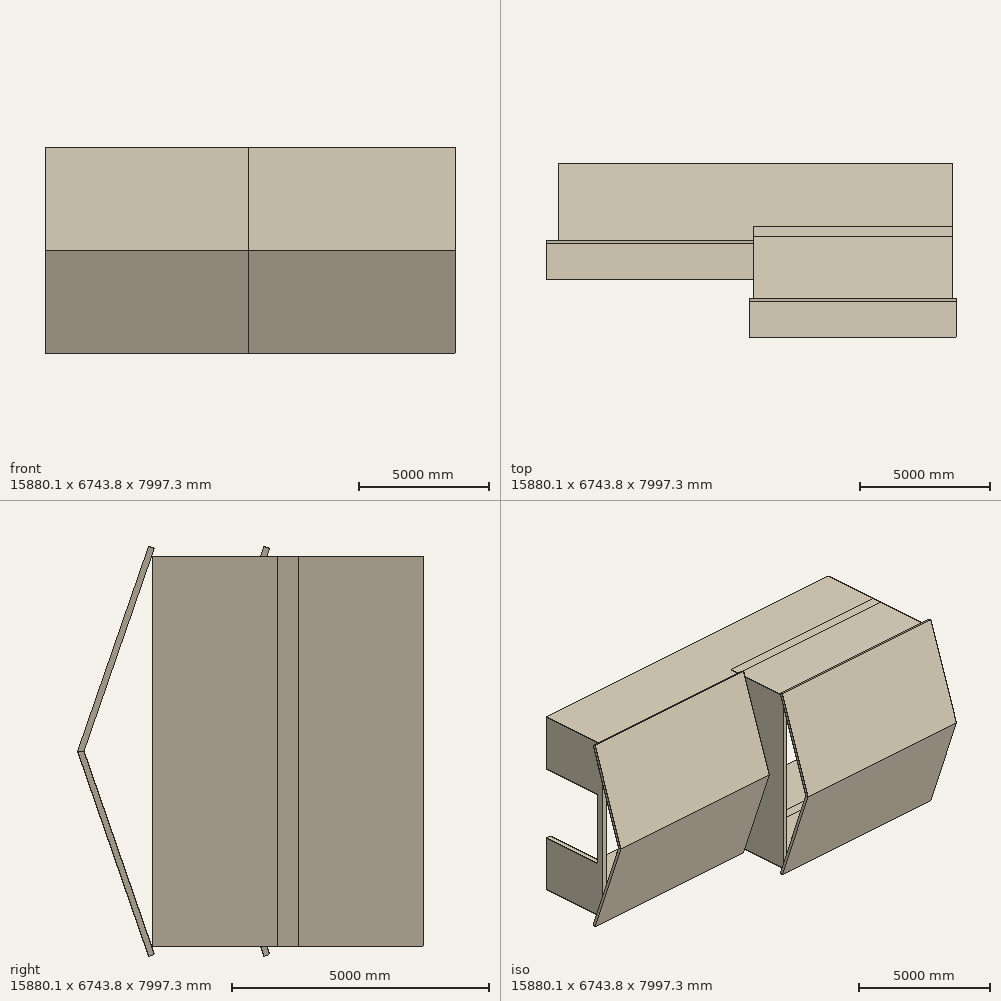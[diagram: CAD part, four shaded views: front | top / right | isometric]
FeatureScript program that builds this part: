
annotation { "Feature Type Name" : "Feature", "Feature Type Description" : "" }
export const myFeature = defineFeature(function(context is Context, id is Id, definition is map)
    precondition{}
    {
        {
            var Q0;
            Q0=qCreatedBy(makeId("Front.planeOp"),FACE);
            var sketch = newSketch(context, id + "F0", { "sketchPlane" : qUnion([Q0])});
            skLineSegment(sketch, "E0.bottom", {"start": v(7620, -3810) * mm, "end": v(-7620, -3810) * mm});
            skLineSegment(sketch, "E0.top", {"start": v(7620, 3810) * mm, "end": v(-7620, 3810) * mm});
            skLineSegment(sketch, "E0.left", {"start": v(7620, -3810) * mm, "end": v(7620, 3810) * mm});
            skLineSegment(sketch, "E0.right", {"start": v(-7620, -3810) * mm, "end": v(-7620, 3810) * mm});
            skPoint(sketch, "E0.middle", {"position": v(0, 0) * mm});
            skLineSegment(sketch, "E1.bottom", {"start": v(7416.8, -3606.8) * mm, "end": v(-7416.8, -3606.8) * mm});
            skLineSegment(sketch, "E1.top", {"start": v(7416.8, 3606.8) * mm, "end": v(-7416.8, 3606.8) * mm});
            skLineSegment(sketch, "E1.left", {"start": v(7416.8, -3606.8) * mm, "end": v(7416.8, 3606.8) * mm});
            skLineSegment(sketch, "E1.right", {"start": v(-7416.8, -3606.8) * mm, "end": v(-7416.8, 3606.8) * mm});
            skLineSegment(sketch, "E2", {"start": v(-76.2, 3810) * mm, "end": v(-76.2, -3810) * mm});
            skLineSegment(sketch, "E3", {"start": v(76.2, 3810) * mm, "end": v(76.2, -3810) * mm});
            skSolve(sketch);
        }
        {
            var Q0;
            {var subQ4=sQuery(id+"F0.wireOp",EDGE,"E0.right");Q0=makeQuery(id+"F0.imprint","IMPRINT",FACE,{"disambiguationData":[TD([[makeQuery(id+"F0.imprint","IMPRINT",EDGE,{"derivedFrom":subQ4}),-1.0]])]});}
            extrude(context, id + "F1", {"entities" : qUnion([Q0]), "depth" : 3048 * mm, "offsetDistance" : 30.48 * mm});
        }
        {
            var Q0;
            {var subQ4=sQuery(id+"F0.wireOp",EDGE,"E0.left");Q0=makeQuery(id+"F0.imprint","IMPRINT",FACE,{"disambiguationData":[TD([[makeQuery(id+"F0.imprint","IMPRINT",EDGE,{"derivedFrom":subQ4}),1.0]])]});}
            var Q1;
            {var subQ0=sQuery(id+"F0.wireOp",EDGE,"E2");var subQ1=sQuery(id+"F0.wireOp",EDGE,"E0.bottom");var subQ2=makeQuery(id+"F0.imprint","INTERSECT",VERTEX,{"derivedFrom":[subQ1,subQ0]});Q1=makeQuery(id+"F0.imprint","IMPRINT",FACE,{"disambiguationData":[TD([[makeQuery(id+"F0.imprint","IMPRINT",EDGE,{"disambiguationData":[TD([[subQ2,1.0]])],"derivedFrom":subQ1}),-1.0]])]});}
            var Q2;
            {var subQ0=sQuery(id+"F0.wireOp",EDGE,"E2");var subQ1=sQuery(id+"F0.wireOp",EDGE,"E0.top");var subQ2=makeQuery(id+"F0.imprint","INTERSECT",VERTEX,{"derivedFrom":[subQ1,subQ0]});Q2=makeQuery(id+"F0.imprint","IMPRINT",FACE,{"disambiguationData":[TD([[makeQuery(id+"F0.imprint","IMPRINT",EDGE,{"disambiguationData":[TD([[subQ2,1.0]])],"derivedFrom":subQ1}),1.0]])]});}
            var Q3;
            {var subQ0=sQuery(id+"F0.wireOp",EDGE,"E3");var subQ1=sQuery(id+"F0.wireOp",EDGE,"E1.bottom");var subQ2=makeQuery(id+"F0.imprint","INTERSECT",VERTEX,{"derivedFrom":[subQ1,subQ0]});Q3=makeQuery(id+"F0.imprint","IMPRINT",FACE,{"disambiguationData":[TD([[makeQuery(id+"F0.imprint","IMPRINT",EDGE,{"disambiguationData":[TD([[subQ2,-1.0]])],"derivedFrom":subQ1}),-1.0]])]});}
            extrude(context, id + "F2", {"entities" : qUnion([Q0, Q1, Q2, Q3]), "operationType" : NewBodyOperationType.ADD, "depth" : 2438.4 * mm, "offsetDistance" : 30.48 * mm});
        }
        {
            var Q0;
            Q0=makeQuery(id+"F2.opExtrude","CAP_FACE",FACE,{"disambiguationData":[OSD([sQuery(id+"F0.wireOp",EDGE,"E0.bottom"),sQuery(id+"F0.wireOp",EDGE,"E0.top"),sQuery(id+"F0.wireOp",EDGE,"E0.left"),sQuery(id+"F0.wireOp",EDGE,"E1.bottom"),sQuery(id+"F0.wireOp",EDGE,"E1.top"),sQuery(id+"F0.wireOp",EDGE,"E1.left"),sQuery(id+"F0.wireOp",EDGE,"gh7um0iQ-zeNB-DT1w-9WpX-ICDftBI5ZBz6")])],"isStart":false});
            extrude(context, id + "F3", {"entities" : qUnion([Q0]), "depth" : 406.4 * mm, "offsetDistance" : 30.48 * mm});
        }
        {
            var Q0;
            Q0=makeQuery(id+"F3.opExtrude","CAP_FACE",FACE,{"disambiguationData":[OSD([sQuery(id+"F0.wireOp",EDGE,"E0.bottom"),sQuery(id+"F0.wireOp",EDGE,"E0.top"),sQuery(id+"F0.wireOp",EDGE,"E0.left"),sQuery(id+"F0.wireOp",EDGE,"E1.bottom"),sQuery(id+"F0.wireOp",EDGE,"E1.top"),sQuery(id+"F0.wireOp",EDGE,"E1.left"),sQuery(id+"F0.wireOp",EDGE,"gh7um0iQ-zeNB-DT1w-9WpX-ICDftBI5ZBz6")])],"isStart":false});
            extrude(context, id + "F4", {"entities" : qUnion([Q0]), "depth" : 2438.4 * mm, "offsetDistance" : 30.48 * mm});
        }
        {
            var Q0;
            Q0=makeQuery(id+"F4.opExtrude","SWEPT_FACE",FACE,{"disambiguationData":[OSD([sQuery(id+"F0.wireOp",EDGE,"E2")])]});
            var sketch = newSketch(context, id + "F5", { "sketchPlane" : qUnion([Q0])});
            skPoint(sketch, "E4", {"position": v(4368.8, 0) * mm});
            skLineSegment(sketch, "E5", {"start": v(4368.8, 0) * mm, "end": v(2996.1, 3959.82) * mm});
            skLineSegment(sketch, "E6", {"start": v(4368.8, 0) * mm, "end": v(4494.34, 0) * mm});
            skLineSegment(sketch, "E7", {"start": v(2996.1, 3959.82) * mm, "end": v(3108.17, 3998.67) * mm});
            skLineSegment(sketch, "E8", {"start": v(3108.17, 3998.67) * mm, "end": v(4494.34, 0) * mm});
            skSolve(sketch);
        }
        {
            var Q0;
            Q0 = qSketchRegion(id + "F5", true);
            var Q1;
            {var subQ0=sQuery(id+"F5.wireOp",EDGE,"E6");Q1=makeQuery(id+"F5.imprint","IMPRINT",FACE,{"disambiguationData":[TD([[makeQuery(id+"F5.imprint","IMPRINT",EDGE,{"derivedFrom":subQ0}),1.0]])]});}
            extrude(context, id + "F6", {"entities" : qUnion([Q0, Q1]), "depth" : 8016.24 * mm, "offsetDistance" : 30.48 * mm});
        }
        {
            var Q0;
            Q0=makeQuery(id+"F6.opExtrude","SWEPT_BODY",BODY,{"disambiguationData":[OSD([sQuery(id+"F5.wireOp",EDGE,"E5"),sQuery(id+"F5.wireOp",EDGE,"E6"),sQuery(id+"F5.wireOp",EDGE,"E7"),sQuery(id+"F5.wireOp",EDGE,"E8")])]});
            var Q1;
            Q1=makeQuery(id+"F6.opExtrude","SWEPT_FACE",FACE,{"disambiguationData":[OSD([sQuery(id+"F5.wireOp",EDGE,"E6")])]});
            mirror(context, id + "F7", {"entities" : qUnion([Q0]), "mirrorPlane" : qUnion([Q1])});
        }
        {
            var Q0;
            Q0=makeQuery(id+"F1.opExtrude","SWEPT_FACE",FACE,{"disambiguationData":[OSD([sQuery(id+"F0.wireOp",EDGE,"E0.right")])]});
            var sketch = newSketch(context, id + "F8", { "sketchPlane" : qUnion([Q0])});
            skLineSegment(sketch, "E9.bottom", {"start": v(0, -1524) * mm, "end": v(2743.2, -1524) * mm});
            skLineSegment(sketch, "E9.top", {"start": v(0, 1524) * mm, "end": v(2743.2, 1524) * mm});
            skLineSegment(sketch, "E9.left", {"start": v(0, -1524) * mm, "end": v(0, 1524) * mm});
            skLineSegment(sketch, "E9.right", {"start": v(2743.2, -1524) * mm, "end": v(2743.2, 1524) * mm});
            skSolve(sketch);
        }
        {
            var Q0;
            Q0 = qSketchRegion(id + "F8", true);
            extrude(context, id + "F9", {"entities" : qUnion([Q0]), "operationType" : NewBodyOperationType.REMOVE, "oppositeDirection" : true, "depth" : 326.14 * mm, "offsetDistance" : 30.48 * mm});
        }
        {
            var Q0;
            Q0=makeQuery(id+"F7.opPattern","COPY",BODY,{"derivedFrom":makeQuery(id+"F6.opExtrude","SWEPT_BODY",BODY,{"disambiguationData":[OSD([sQuery(id+"F5.wireOp",EDGE,"E5"),sQuery(id+"F5.wireOp",EDGE,"E6"),sQuery(id+"F5.wireOp",EDGE,"E7"),sQuery(id+"F5.wireOp",EDGE,"E8")])]}),"instanceName":"1"});
            transform(context, id + "F10", {"entities" : qUnion([Q0]), "transformType" : TransformType.TRANSLATION_3D, "dx" : 7863.84 * mm, "dy" : -2249.42 * mm, "dz" : 0 * mm, "makeCopy" : true});
        }
        {
            var Q0;
            Q0=makeQuery(id+"F10.opPattern","COPY",BODY,{"derivedFrom":makeQuery(id+"F7.opPattern","COPY",BODY,{"derivedFrom":makeQuery(id+"F6.opExtrude","SWEPT_BODY",BODY,{"disambiguationData":[OSD([sQuery(id+"F5.wireOp",EDGE,"E5"),sQuery(id+"F5.wireOp",EDGE,"E6"),sQuery(id+"F5.wireOp",EDGE,"E7"),sQuery(id+"F5.wireOp",EDGE,"E8")])]}),"instanceName":"1"}),"instanceName":"1"});
            var Q1;
            Q1=makeQuery(id+"F10.opPattern","COPY",FACE,{"derivedFrom":makeQuery(id+"F7.opPattern","COPY",FACE,{"derivedFrom":makeQuery(id+"F6.opExtrude","SWEPT_FACE",FACE,{"disambiguationData":[OSD([sQuery(id+"F5.wireOp",EDGE,"E6")])]}),"instanceName":"1"}),"instanceName":"1"});
            mirror(context, id + "F11", {"operationType" : NewBodyOperationType.ADD, "entities" : qUnion([Q0]), "mirrorPlane" : qUnion([Q1])});
        }
    });
